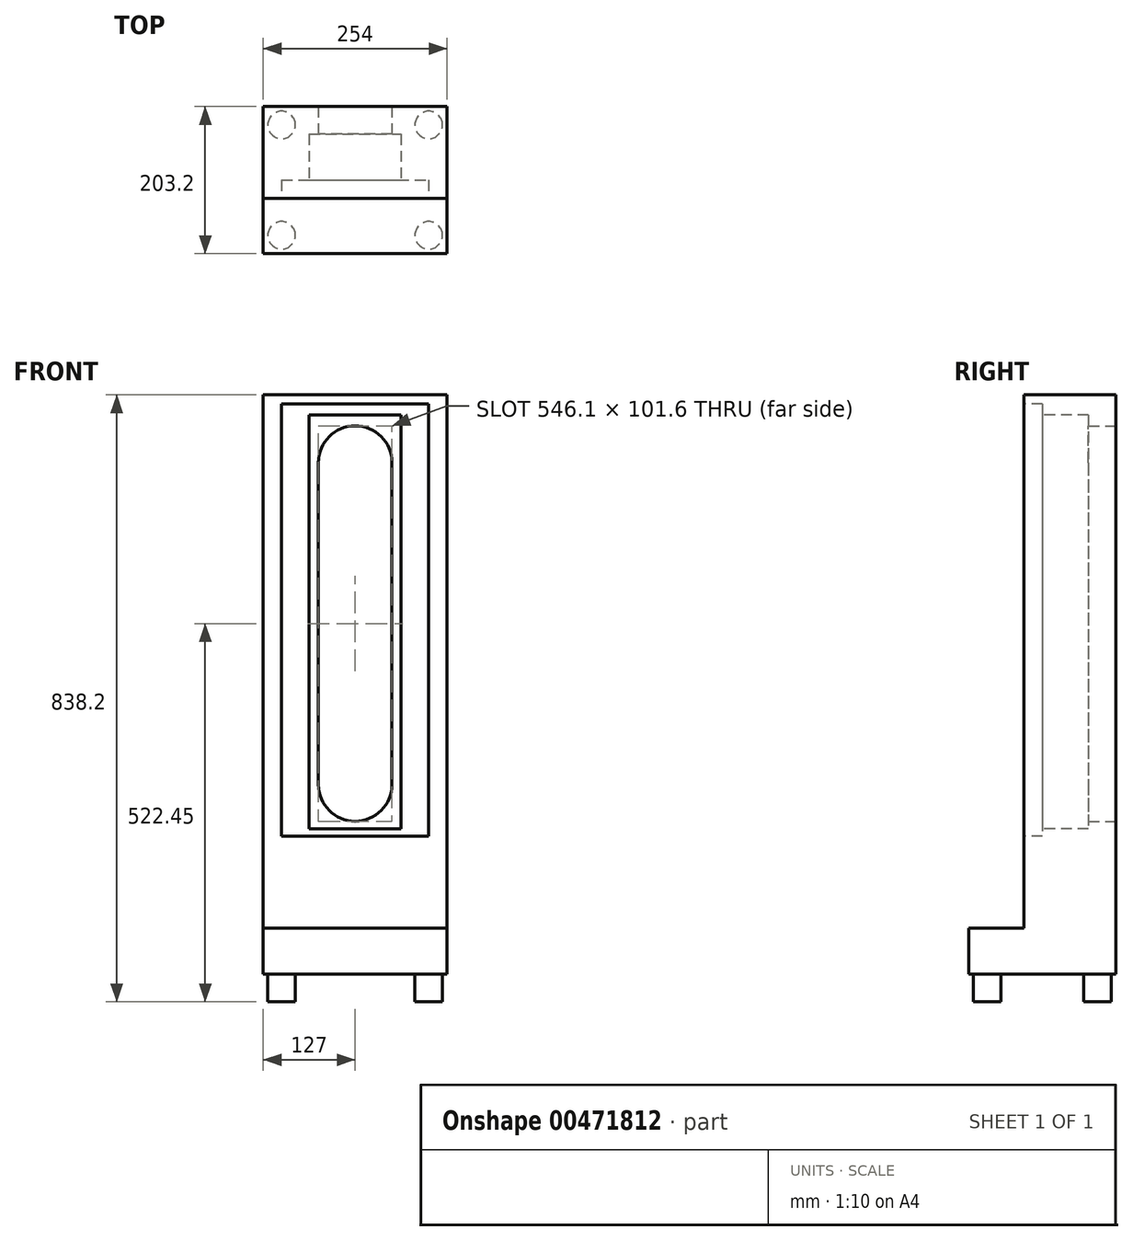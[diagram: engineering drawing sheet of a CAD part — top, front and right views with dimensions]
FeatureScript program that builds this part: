
annotation { "Feature Type Name" : "Feature", "Feature Type Description" : "" }
export const myFeature = defineFeature(function(context is Context, id is Id, definition is map)
    precondition{}
    {
        {
            var Q0;
            Q0=qCreatedBy(makeId("Front.planeOp"),FACE);
            var sketch = newSketch(context, id + "F0", { "sketchPlane" : qUnion([Q0])});
            skLineSegment(sketch, "E0.top", {"start": v(127, 609.6) * mm, "end": v(-127, 609.6) * mm});
            skLineSegment(sketch, "E0.left", {"start": v(127, -190.5) * mm, "end": v(127, 609.6) * mm});
            skLineSegment(sketch, "E0.right", {"start": v(-127, -190.5) * mm, "end": v(-127, 609.6) * mm});
            skPoint(sketch, "E1.middle", {"position": v(0, 0) * mm});
            skLineSegment(sketch, "E2", {"start": v(-127, -190.5) * mm, "end": v(127, -190.5) * mm});
            skPoint(sketch, "E3.orphan", {"position": v(-127, -609.6) * mm});
            skPoint(sketch, "E4.orphan", {"position": v(127, -609.6) * mm});
            skLineSegment(sketch, "E5.bottom", {"start": v(-101.6, 596.9) * mm, "end": v(101.6, 596.9) * mm});
            skLineSegment(sketch, "E5.top", {"start": v(-101.6, 0) * mm, "end": v(101.6, 0) * mm});
            skLineSegment(sketch, "E5.left", {"start": v(-101.6, 596.9) * mm, "end": v(-101.6, 0) * mm});
            skLineSegment(sketch, "E5.right", {"start": v(101.6, 596.9) * mm, "end": v(101.6, 0) * mm});
            skLineSegment(sketch, "E6.bottom", {"start": v(-63.5, 581.9) * mm, "end": v(63.5, 581.9) * mm});
            skLineSegment(sketch, "E6.top", {"start": v(-63.5, 10.4) * mm, "end": v(63.5, 10.4) * mm});
            skLineSegment(sketch, "E6.left", {"start": v(-63.5, 581.9) * mm, "end": v(-63.5, 10.4) * mm});
            skLineSegment(sketch, "E6.right", {"start": v(63.5, 581.9) * mm, "end": v(63.5, 10.4) * mm});
            skLineSegment(sketch, "E7.bottom", {"start": v(-50.8, 566.9) * mm, "end": v(50.8, 566.9) * mm});
            skLineSegment(sketch, "E7.top", {"start": v(-50.8, 20.8) * mm, "end": v(50.8, 20.8) * mm});
            skLineSegment(sketch, "E7.left", {"start": v(-50.8, 566.9) * mm, "end": v(-50.8, 20.8) * mm});
            skLineSegment(sketch, "E7.right", {"start": v(50.8, 566.9) * mm, "end": v(50.8, 20.8) * mm});
            skLineSegment(sketch, "E8", {"start": v(0, 870.13) * mm, "end": v(0, -870.13) * mm, "construction": true});
            skLineSegment(sketch, "E9.top", {"start": v(-127, -127) * mm, "end": v(127, -127) * mm});
            skLineSegment(sketch, "E9.left", {"start": v(-127, -190.5) * mm, "end": v(-127, -127) * mm});
            skLineSegment(sketch, "E9.right", {"start": v(127, -190.5) * mm, "end": v(127, -127) * mm});
            skSolve(sketch);
        }
        {
            var Q0;
            Q0=makeQuery(id+"F0.imprint","IMPRINT",FACE,{"disambiguationData":[TD([[makeQuery(id+"F0.imprint","IMPRINT",EDGE,{"derivedFrom":sQuery(id+"F0.wireOp",EDGE,"E0.top")}),1.0]])]});
            var Q1;
            Q1=makeQuery(id+"F0.imprint","IMPRINT",FACE,{"disambiguationData":[TD([[makeQuery(id+"F0.imprint","IMPRINT",EDGE,{"derivedFrom":sQuery(id+"F0.wireOp",EDGE,"E1.bottom")}),-1.0]])]});
            var Q2;
            Q2=makeQuery(id+"F0.imprint","IMPRINT",FACE,{"disambiguationData":[TD([[makeQuery(id+"F0.imprint","IMPRINT",EDGE,{"derivedFrom":sQuery(id+"F0.wireOp",EDGE,"l2cz76WN-11cX-8Qg5-Wc74-vKwfhGCtYGeO.bottom")}),-1.0]])]});
            var Q3;
            {var subQ0=sQuery(id+"F0.wireOp",EDGE,"dQK7Thth-TP6K-kbBQ-5Cwl-0GHNaYrmpQfn.left");var subQ1=sQuery(id+"F0.wireOp",EDGE,"E1.bottom");var subQ2=makeQuery(id+"F0.imprint","INTERSECT",VERTEX,{"derivedFrom":[subQ1,subQ0]});Q3=makeQuery(id+"F0.imprint","IMPRINT",FACE,{"disambiguationData":[TD([[makeQuery(id+"F0.imprint","IMPRINT",EDGE,{"disambiguationData":[TD([[subQ2,-1.0]])],"derivedFrom":subQ1}),1.0]])]});}
            var Q4;
            {var subQ5=sQuery(id+"F0.wireOp",EDGE,"huDVYpq4-8GHm-f6ov-cYvV-LWDsyoBmHsaB.top");Q4=makeQuery(id+"F0.imprint","IMPRINT",FACE,{"disambiguationData":[TD([[makeQuery(id+"F0.imprint","IMPRINT",EDGE,{"derivedFrom":subQ5}),1.0]])]});}
            var Q5;
            {var subQ5=sQuery(id+"F0.wireOp",EDGE,"dQK7Thth-TP6K-kbBQ-5Cwl-0GHNaYrmpQfn.bottom");Q5=makeQuery(id+"F0.imprint","IMPRINT",FACE,{"disambiguationData":[TD([[makeQuery(id+"F0.imprint","IMPRINT",EDGE,{"derivedFrom":subQ5}),-1.0]])]});}
            var Q6;
            {var subQ5=sQuery(id+"F0.wireOp",EDGE,"dQK7Thth-TP6K-kbBQ-5Cwl-0GHNaYrmpQfn.top");Q6=makeQuery(id+"F0.imprint","IMPRINT",FACE,{"disambiguationData":[TD([[makeQuery(id+"F0.imprint","IMPRINT",EDGE,{"derivedFrom":subQ5}),1.0]])]});}
            var Q7;
            {var subQ5=sQuery(id+"F0.wireOp",EDGE,"huDVYpq4-8GHm-f6ov-cYvV-LWDsyoBmHsaB.bottom");Q7=makeQuery(id+"F0.imprint","IMPRINT",FACE,{"disambiguationData":[TD([[makeQuery(id+"F0.imprint","IMPRINT",EDGE,{"derivedFrom":subQ5}),-1.0]])]});}
            var Q8;
            {var subQ0=sQuery(id+"F0.wireOp",EDGE,"dQK7Thth-TP6K-kbBQ-5Cwl-0GHNaYrmpQfn.left");var subQ1=sQuery(id+"F0.wireOp",EDGE,"E1.bottom");var subQ2=makeQuery(id+"F0.imprint","INTERSECT",VERTEX,{"derivedFrom":[subQ1,subQ0]});Q8=makeQuery(id+"F0.imprint","IMPRINT",FACE,{"disambiguationData":[TD([[makeQuery(id+"F0.imprint","IMPRINT",EDGE,{"disambiguationData":[TD([[subQ2,-1.0]])],"derivedFrom":subQ1}),-1.0]])]});}
            var Q9;
            Q9=makeQuery(id+"F0.imprint","IMPRINT",FACE,{"disambiguationData":[TD([[makeQuery(id+"F0.imprint","IMPRINT",EDGE,{"derivedFrom":sQuery(id+"F0.wireOp",EDGE,"E6.bottom")}),-1.0]])]});
            var Q10;
            Q10=makeQuery(id+"F0.imprint","IMPRINT",FACE,{"disambiguationData":[TD([[makeQuery(id+"F0.imprint","IMPRINT",EDGE,{"derivedFrom":sQuery(id+"F0.wireOp",EDGE,"E5.bottom")}),-1.0]])]});
            var Q11;
            Q11=makeQuery(id+"F0.imprint","IMPRINT",FACE,{"disambiguationData":[TD([[makeQuery(id+"F0.imprint","IMPRINT",EDGE,{"derivedFrom":sQuery(id+"F0.wireOp",EDGE,"E2")}),1.0]])]});
            extrude(context, id + "F1", {"entities" : qUnion([Q0, Q1, Q2, Q3, Q4, Q5, Q6, Q7, Q8, Q9, Q10, Q11]), "oppositeDirection" : true, "depth" : 127 * mm});
        }
        {
            var Q0;
            Q0=makeQuery(id+"F0.imprint","IMPRINT",FACE,{"disambiguationData":[TD([[makeQuery(id+"F0.imprint","IMPRINT",EDGE,{"derivedFrom":sQuery(id+"F0.wireOp",EDGE,"E5.bottom")}),-1.0]])]});
            extrude(context, id + "F2", {"entities" : qUnion([Q0]), "operationType" : NewBodyOperationType.REMOVE, "oppositeDirection" : true, "depth" : 25.4 * mm});
        }
        {
            var Q0;
            Q0=makeQuery(id+"F0.imprint","IMPRINT",FACE,{"disambiguationData":[TD([[makeQuery(id+"F0.imprint","IMPRINT",EDGE,{"derivedFrom":sQuery(id+"F0.wireOp",EDGE,"E6.bottom")}),-1.0]])]});
            extrude(context, id + "F3", {"entities" : qUnion([Q0]), "operationType" : NewBodyOperationType.REMOVE, "oppositeDirection" : true, "depth" : 88.9 * mm});
        }
        {
            var Q0;
            Q0=makeQuery(id+"F1.opExtrude","SWEPT_EDGE",EDGE,{"disambiguationData":[OSD([sQuery(id+"F0.wireOp",EDGE,"E7.bottom"),sQuery(id+"F0.wireOp",EDGE,"E7.right")])]});
            var Q1;
            Q1=makeQuery(id+"F1.opExtrude","SWEPT_EDGE",EDGE,{"disambiguationData":[OSD([sQuery(id+"F0.wireOp",EDGE,"E7.bottom"),sQuery(id+"F0.wireOp",EDGE,"E7.left")])]});
            var Q2;
            Q2=makeQuery(id+"F1.opExtrude","SWEPT_EDGE",EDGE,{"disambiguationData":[OSD([sQuery(id+"F0.wireOp",EDGE,"E7.top"),sQuery(id+"F0.wireOp",EDGE,"E7.left")])]});
            var Q3;
            Q3=makeQuery(id+"F1.opExtrude","SWEPT_EDGE",EDGE,{"disambiguationData":[OSD([sQuery(id+"F0.wireOp",EDGE,"E7.top"),sQuery(id+"F0.wireOp",EDGE,"E7.right")])]});
            fillet(context, id + "F4", {"entities" : qUnion([Q0, Q1, Q2, Q3]), "radius" : 50.8 * mm, "tangentPropagation" : true, "allowEdgeOverflow" : false});
        }
        {
            var Q0;
            Q0=makeQuery(id+"F0.imprint","IMPRINT",FACE,{"disambiguationData":[TD([[makeQuery(id+"F0.imprint","IMPRINT",EDGE,{"derivedFrom":sQuery(id+"F0.wireOp",EDGE,"E2")}),1.0]])]});
            extrude(context, id + "F5", {"entities" : qUnion([Q0]), "operationType" : NewBodyOperationType.ADD, "depth" : 76.2 * mm});
        }
        {
            var Q0;
            {var subQ0=sQuery(id+"F0.wireOp",EDGE,"E2");Q0=makeQuery(id+"F5.boolean.opBoolean","MERGE",FACE,{"derivedFrom":[makeQuery(id+"F1.opExtrude","SWEPT_FACE",FACE,{"disambiguationData":[OSD([subQ0])]}),makeQuery(id+"F5.opExtrude","SWEPT_FACE",FACE,{"disambiguationData":[OSD([subQ0])]})]});}
            var sketch = newSketch(context, id + "F6", { "sketchPlane" : qUnion([Q0])});
            skCircle(sketch, "E10", {"center": v(-101.6, 50.8) * mm, "radius": 19.05 * mm});
            skCircle(sketch, "E11", {"center": v(101.6, 50.8) * mm, "radius": 19.05 * mm});
            skCircle(sketch, "E12", {"center": v(-101.6, -101.6) * mm, "radius": 19.05 * mm});
            skCircle(sketch, "E13", {"center": v(101.6, -101.6) * mm, "radius": 19.05 * mm});
            skSolve(sketch);
        }
        {
            var Q0;
            Q0=qSketchRegion(id+"F6",true);
            extrude(context, id + "F7", {"entities" : qUnion([Q0]), "operationType" : NewBodyOperationType.ADD, "depth" : 38.1 * mm});
        }
    });
